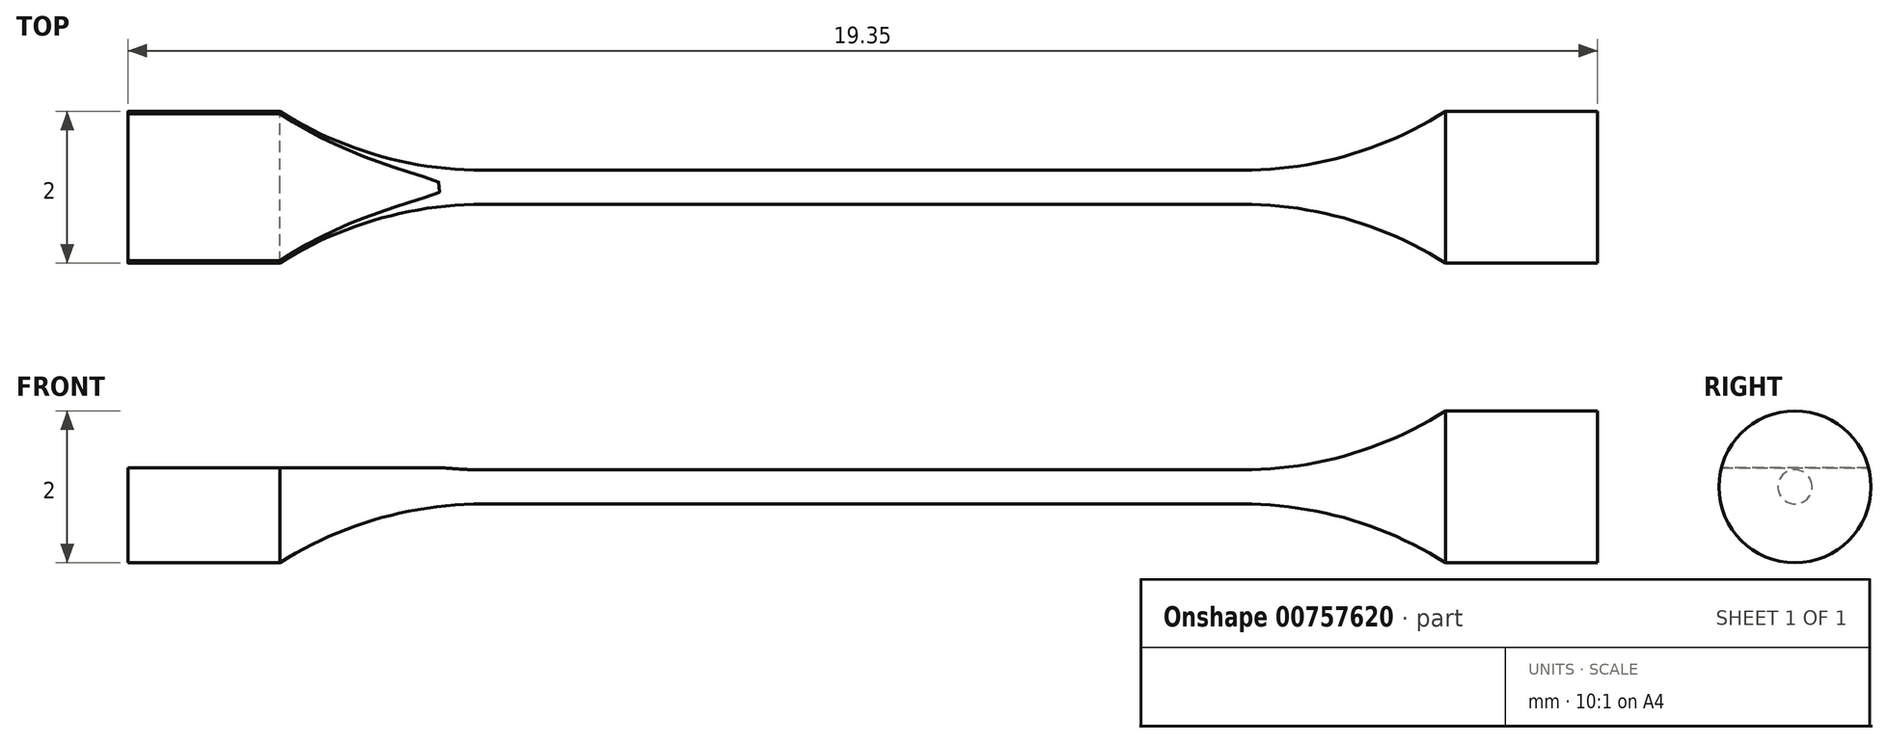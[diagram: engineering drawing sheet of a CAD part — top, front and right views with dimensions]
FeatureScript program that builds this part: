
annotation { "Feature Type Name" : "Feature", "Feature Type Description" : "" }
export const myFeature = defineFeature(function(context is Context, id is Id, definition is map)
    precondition{}
    {
        {
            var Q0;
            Q0=qCreatedBy(makeId("Front.planeOp"),FACE);
            var sketch = newSketch(context, id + "F0", { "sketchPlane" : qUnion([Q0])});
            skLineSegment(sketch, "E0", {"start": v(0, 0) * mm, "end": v(0, 1) * mm});
            skLineSegment(sketch, "E1", {"start": v(0, 1) * mm, "end": v(2, 1) * mm});
            skArc(sketch, "E2", {"start": v(2, 1) * mm, "mid": v(3.28, 0.42) * mm, "end": v(4.67, 0.22) * mm});
            skLineSegment(sketch, "E3", {"start": v(4.67, 0.23) * mm, "end": v(9.67, 0.23) * mm});
            skLineSegment(sketch, "E4", {"start": v(0, 0) * mm, "end": v(9.67, 0) * mm});
            skLineSegment(sketch, "E5", {"start": v(9.67, 0) * mm, "end": v(9.67, 1.54) * mm, "construction": true});
            skLineSegment(sketch, "E6.MirrorCS", {"start": v(19.35, 1) * mm, "end": v(17.35, 1) * mm});
            skArc(sketch, "E7.MirrorCS", {"start": v(17.35, 1) * mm, "mid": v(16.07, 0.42) * mm, "end": v(14.67, 0.23) * mm});
            skLineSegment(sketch, "E8.MirrorCS", {"start": v(19.35, 0) * mm, "end": v(19.35, 1) * mm});
            skLineSegment(sketch, "E9.MirrorCS", {"start": v(14.67, 0.23) * mm, "end": v(9.67, 0.23) * mm});
            skLineSegment(sketch, "E10.MirrorCS", {"start": v(19.35, 0) * mm, "end": v(9.67, 0) * mm});
            skLineSegment(sketch, "E11", {"start": v(9.67, 0) * mm, "end": v(-2.75, 0) * mm, "construction": true});
            skSolve(sketch);
        }
        {
            var Q0;
            Q0=makeQuery(id+"F0.imprint","IMPRINT",FACE,{"disambiguationData":[TD([[makeQuery(id+"F0.imprint","IMPRINT",EDGE,{"derivedFrom":sQuery(id+"F0.wireOp",EDGE,"E0")}),-1.0]])]});
            var Q1;
            Q1=sQuery(id+"F0.wireOp",EDGE,"E11");
            revolve(context, id + "F1", {"surfaceOperationType" : NewSurfaceOperationType.NEW, "entities" : qUnion([Q0]), "axis" : qUnion([Q1]), "revolveType" : RevolveType.FULL});
        }
        {
            var Q0;
            Q0=qCreatedBy(makeId("Top.planeOp"),FACE);
            cPlane(context, id + "F2", {"entities" : qUnion([Q0]), "cplaneType" : CPlaneType.OFFSET, "offset" : 2.6 * mm, "width" : 150 * mm, "height" : 150 * mm});
        }
        {
            var Q0;
            Q0=qCreatedBy(id+"F2.planeOp",FACE);
            var sketch = newSketch(context, id + "F3", { "sketchPlane" : qUnion([Q0])});
            skLineSegment(sketch, "E12.bottom", {"start": v(-0.59, -1.55) * mm, "end": v(4.98, -1.55) * mm});
            skLineSegment(sketch, "E12.top", {"start": v(-0.59, 1.75) * mm, "end": v(4.98, 1.75) * mm});
            skLineSegment(sketch, "E12.left", {"start": v(-0.59, -1.55) * mm, "end": v(-0.59, 1.75) * mm});
            skLineSegment(sketch, "E12.right", {"start": v(4.98, -1.55) * mm, "end": v(4.98, 1.75) * mm});
            skSolve(sketch);
        }
        {
            var Q0;
            Q0=makeQuery(id+"F3.imprint","IMPRINT",FACE,{"disambiguationData":[TD([[makeQuery(id+"F3.imprint","IMPRINT",EDGE,{"derivedFrom":sQuery(id+"F3.wireOp",EDGE,"E12.bottom")}),1.0]])]});
            extrude(context, id + "F4", {"entities" : qUnion([Q0]), "operationType" : NewBodyOperationType.REMOVE, "oppositeDirection" : true, "depth" : 2.35 * mm, "offsetDistance" : 25 * mm});
        }
    });
